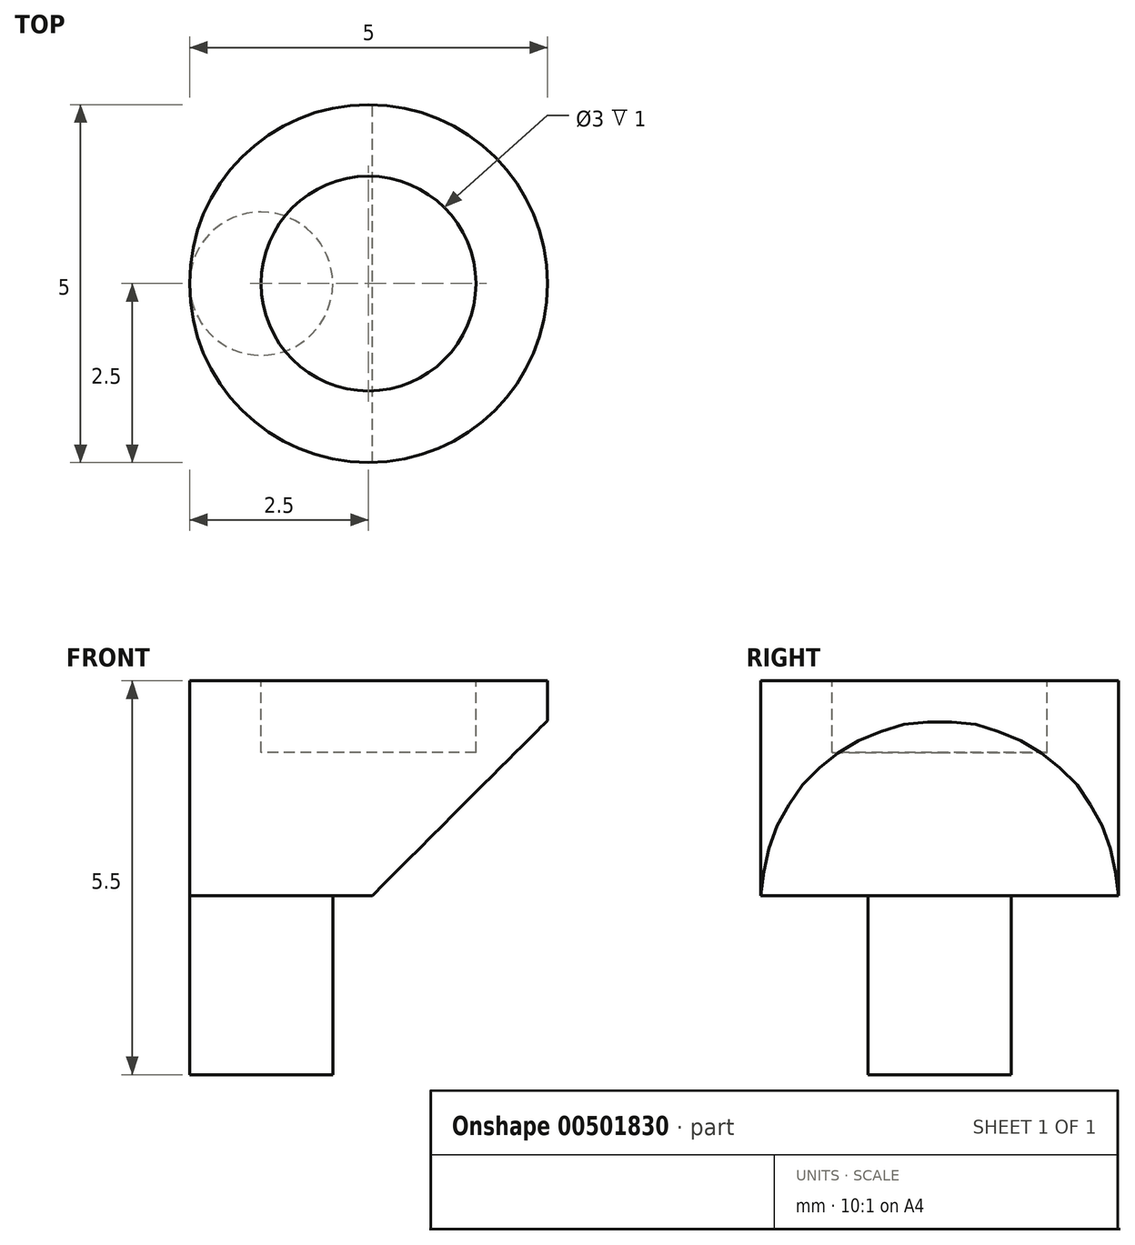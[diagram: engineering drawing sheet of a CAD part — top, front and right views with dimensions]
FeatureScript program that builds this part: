
annotation { "Feature Type Name" : "Feature", "Feature Type Description" : "" }
export const myFeature = defineFeature(function(context is Context, id is Id, definition is map)
    precondition{}
    {
        {
            var Q0;
            Q0=qCreatedBy(makeId("Top.planeOp"),FACE);
            var sketch = newSketch(context, id + "F0", { "sketchPlane" : qUnion([Q0])});
            skCircle(sketch, "E0", {"center": v(0, 0) * mm, "radius": 2.5 * mm});
            skSolve(sketch);
        }
        {
            var Q0;
            Q0 = qSketchRegion(id + "F0", true);
            extrude(context, id + "F1", {"entities" : qUnion([Q0]), "depth" : 3 * mm});
        }
        {
            var Q0;
            Q0=qCreatedBy(makeId("Front.planeOp"),FACE);
            var sketch = newSketch(context, id + "F2", { "sketchPlane" : qUnion([Q0])});
            skLineSegment(sketch, "E1", {"start": v(-4.79, -4.84) * mm, "end": v(6.73, 6.67) * mm});
            skLineSegment(sketch, "E2", {"start": v(6.73, 6.67) * mm, "end": v(6.73, -4.84) * mm});
            skLineSegment(sketch, "E3", {"start": v(6.73, -4.84) * mm, "end": v(-4.79, -4.84) * mm});
            skSolve(sketch);
        }
        {
            var Q0;
            Q0 = qSketchRegion(id + "F2", true);
            extrude(context, id + "F3", {"entities" : qUnion([Q0]), "operationType" : NewBodyOperationType.REMOVE, "oppositeDirection" : true, "depth" : 25 * mm, "hasSecondDirection" : true, "secondDirectionOppositeDirection" : false, "secondDirectionDepth" : 25 * mm});
        }
        {
            var Q0;
            Q0=makeQuery(id+"F1.opExtrude","CAP_FACE",FACE,{"disambiguationData":[OSD([sQuery(id+"F0.wireOp",EDGE,"E0")])],"isStart":true});
            var sketch = newSketch(context, id + "F4", { "sketchPlane" : qUnion([Q0])});
            skCircle(sketch, "E4", {"center": v(-1.5, 0) * mm, "radius": 1 * mm});
            skSolve(sketch);
        }
        {
            var Q0;
            Q0 = qSketchRegion(id + "F4", true);
            extrude(context, id + "F5", {"entities" : qUnion([Q0]), "operationType" : NewBodyOperationType.ADD, "depth" : 2.5 * mm});
        }
        {
            var Q0;
            Q0=makeQuery(id+"F1.opExtrude","CAP_FACE",FACE,{"disambiguationData":[OSD([sQuery(id+"F0.wireOp",EDGE,"E0")])],"isStart":false});
            var sketch = newSketch(context, id + "F6", { "sketchPlane" : qUnion([Q0])});
            skCircle(sketch, "E5", {"center": v(0, 0) * mm, "radius": 1.5 * mm});
            skSolve(sketch);
        }
        {
            var Q0;
            Q0 = qSketchRegion(id + "F6", true);
            extrude(context, id + "F7", {"entities" : qUnion([Q0]), "operationType" : NewBodyOperationType.REMOVE, "oppositeDirection" : true, "depth" : 1 * mm});
        }
    });
